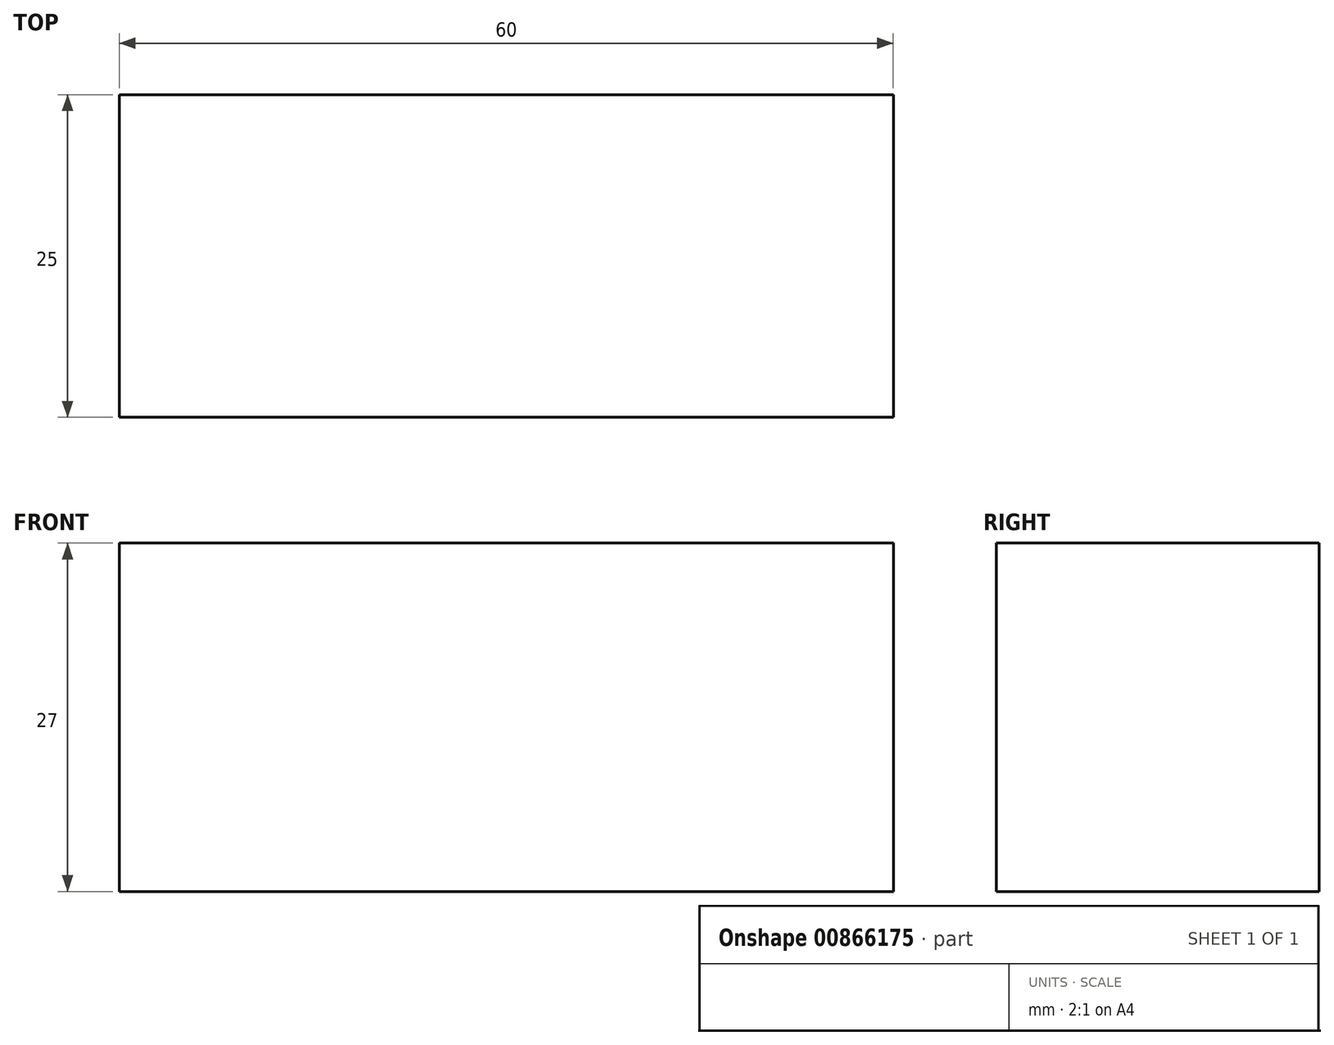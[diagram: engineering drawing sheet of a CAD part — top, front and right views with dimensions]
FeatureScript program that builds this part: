
annotation { "Feature Type Name" : "Feature", "Feature Type Description" : "" }
export const myFeature = defineFeature(function(context is Context, id is Id, definition is map)
    precondition{}
    {
        {
            var Q0;
            Q0=qCreatedBy(makeId("Front.planeOp"),FACE);
            var sketch = newSketch(context, id + "F0", { "sketchPlane" : qUnion([Q0])});
            skLineSegment(sketch, "E0.bottom", {"start": v(-51.19, 22.09) * mm, "end": v(8.81, 22.09) * mm});
            skLineSegment(sketch, "E0.top", {"start": v(-51.19, -4.91) * mm, "end": v(8.81, -4.91) * mm});
            skLineSegment(sketch, "E0.left", {"start": v(-51.19, 22.09) * mm, "end": v(-51.19, -4.91) * mm});
            skLineSegment(sketch, "E0.right", {"start": v(8.81, 22.09) * mm, "end": v(8.81, -4.91) * mm});
            skSolve(sketch);
        }
        {
            var Q0;
            Q0 = qSketchRegion(id + "F0", true);
            extrude(context, id + "F1", {"entities" : qUnion([Q0]), "depth" : 25 * mm, "offsetDistance" : 25 * mm});
        }
    });
